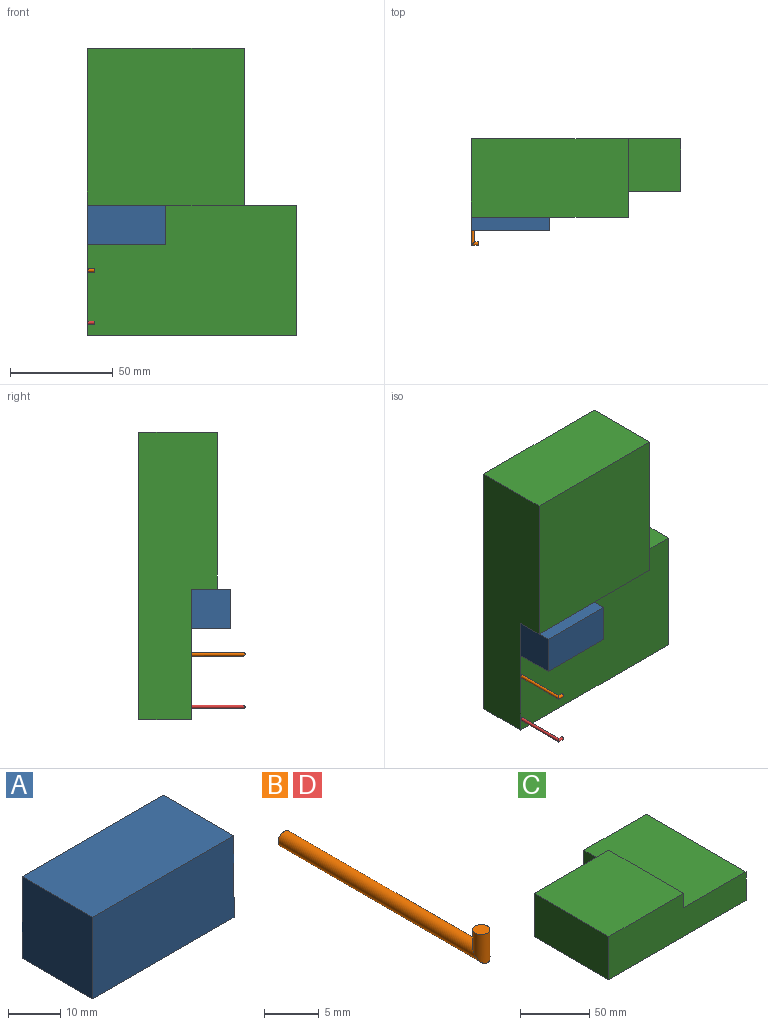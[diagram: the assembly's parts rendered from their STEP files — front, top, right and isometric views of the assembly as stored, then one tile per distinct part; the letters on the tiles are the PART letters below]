
ASSEMBLY  parts=4 mates=3
PART A: 11 faces, bbox 38.1x19.1x19.1 mm
  f0: plane 19.05x19.05mm, normal (1,0,0), area 106.8mm2, adj f1,f2,f3,f4,f6,f7,f8,f9
  f1: plane 38.1x19.05mm, normal (0,0,-1), area 725.8mm2, adj f0,f2,f4,f5
  f2: plane 38.1x19.05mm, normal (0,1,0), area 725.8mm2, adj f0,f1,f3,f5
  f3: plane 38.1x19.05mm, normal (0,0,1), area 725.8mm2, adj f0,f2,f4,f5
  f4: plane 38.1x19.05mm, normal (0,-1,0), area 725.8mm2, adj f0,f1,f3,f5
  f5: plane 19.05x19.05mm, normal (-1,0,0), area 362.9mm2, adj f1,f2,f3,f4
  f6: plane 36.58x16mm, normal (0,0,1), area 585.3mm2, adj f0,f7,f9,f10
  f7: plane 36.58x16mm, normal (0,-1,0), area 585.3mm2, adj f0,f6,f8,f10
  f8: plane 36.58x16mm, normal (0,0,-1), area 585.3mm2, adj f0,f7,f9,f10
  f9: plane 36.58x16mm, normal (0,1,0), area 585.3mm2, adj f0,f6,f8,f10
  f10: plane 16x16mm, normal (1,0,0), area 256.1mm2, adj f6,f7,f8,f9
PART B: 4 faces, bbox 1.6x26.2x3.3 mm
  f0: plane 1.59x1.59mm, normal (0,0,1), area 2mm2, adj f2
  f1: plane 1.59x1.59mm, normal (0,1,0), area 2mm2, adj f3
  f2: cylinder r=0.79mm len=3.33mm, axis (0,0,1), area 12.7mm2, adj f0,f3
  f3: cylinder r=0.79mm len=26.19mm, axis (0,-1,0), area 126.7mm2, adj f1,f2
PART C: 27 faces, bbox 139.7x101.6x38.1 mm
  f0: plane 63.5x25.4mm, normal (0,1,0), area 295.7mm2, adj f6,f12,f13,f17,f18,f19,f20,f21
  f1: plane 76.2x12.7mm, normal (1,0,0), area 967.7mm2, adj f2,f3,f5,f13
  f2: plane 76.2x38.1mm, normal (0,1,0), area 339.1mm2, adj f1,f4,f5,f6,f8,f9,f10,f11
  f3: plane 139.7x38.1mm, normal (0,-1,0), area 4516.1mm2, adj f1,f4,f5,f6,f13,f21
  f4: plane 76.2x38.1mm, normal (-1,0,0), area 2903.2mm2, adj f2,f3,f5,f6
  f5: plane 76.2x76.2mm, normal (0,0,1), area 5806.4mm2, adj f1,f2,f3,f4
  f6: plane 139.7x101.6mm, normal (0,0,-1), area 12258mm2, adj f0,f2,f3,f4,f12,f21
  f7: plane 73.15x35.05mm, normal (0,1,0), area 2564.1mm2, adj f8,f9,f10,f11
  f8: plane 74.68x35.05mm, normal (-1,0,0), area 2617.5mm2, adj f2,f7,f10,f11
  f9: plane 74.68x35.05mm, normal (1,0,0), area 2617.5mm2, adj f2,f7,f10,f11
  f10: plane 74.68x73.15mm, normal (0,0,-1), area 5462.7mm2, adj f2,f7,f8,f9
  f11: plane 74.68x73.15mm, normal (0,0,1), area 5462.7mm2, adj f2,f7,f8,f9
  f12: plane 25.4x25.4mm, normal (-1,0,0), area 645.2mm2, adj f0,f2,f6,f13
  f13: plane 101.6x63.5mm, normal (0,0,1), area 6451.6mm2, adj f0,f1,f3,f12,f21
  f14: plane 73.15x22.35mm, normal (1,0,0), area 1635.1mm2, adj f15,f16,f17,f20
  f15: plane 22.35x1.52mm, normal (0,-1,0), area 34.1mm2, adj f14,f17,f18,f20
  f16: plane 42.93x22.35mm, normal (0,1,0), area 959.5mm2, adj f14,f17,f19,f20
  f17: plane 100.08x42.93mm, normal (0,0,1), area 4254.8mm2, adj f0,f14,f15,f16,f18,f19
  f18: plane 26.92x22.35mm, normal (1,0,0), area 601.8mm2, adj f0,f15,f17,f20
  f19: plane 100.08x22.35mm, normal (-1,0,0), area 2236.9mm2, adj f0,f16,f17,f20
  f20: plane 100.08x42.93mm, normal (0,0,-1), area 4254.8mm2, adj f0,f14,f15,f16,f18,f19
  f21: plane 101.6x25.4mm, normal (1,0,0), area 2580.6mm2, adj f0,f3,f6,f13
  f22: plane 22.35x17.53mm, normal (0,1,0), area 391.7mm2, adj f23,f24,f25,f26
  f23: plane 100.08x17.53mm, normal (0,0,1), area 1753.9mm2, adj f0,f22,f25,f26
  f24: plane 100.08x17.53mm, normal (0,0,-1), area 1753.9mm2, adj f0,f22,f25,f26
  f25: plane 100.08x22.35mm, normal (1,0,0), area 2236.9mm2, adj f0,f22,f23,f24
  f26: plane 100.08x22.35mm, normal (-1,0,0), area 2236.9mm2, adj f0,f22,f23,f24
PART D: same geometry as B
PLACE A t=(-157.73,-168.72,66.53)mm
PLACE B rot(axis=(0,1,0),90deg) t=(-156.93,-149.67,53.83)mm
PLACE C rot(axis=(0.58,0.58,-0.58),120deg) t=(-119.63,-124.27,91.93)mm
PLACE D rot(axis=(0,1,0),90deg) t=(-156.93,-149.67,28.43)mm
MATE fastened D.f3 <-> C.f13  axis (0,1,0) through (-156.93,-149.67,28.43)mm
MATE fastened C.f13 <-> A.f2  axis (0,-1,0) through (-157.73,-149.67,85.58)mm
MATE fastened B.f3 <-> C.f13  axis (0,1,0) through (-156.93,-149.67,53.83)mm
